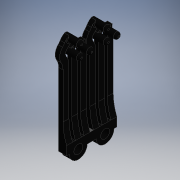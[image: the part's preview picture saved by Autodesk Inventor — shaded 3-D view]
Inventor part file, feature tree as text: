
AUTODESK INVENTOR PART (.ipt)
format: ipt  version: 2016 (Build 200138000, 138)  size: 284,672 bytes
history: native  units: mm (DEFAULTED — no unit token found)
features: other x3, extrude x1, sketch x1
ambient origin geometry x8: Origin, YZ Plane, XZ Plane, XY Plane, X Axis, Y Axis, Z Axis, Center Point
bodies: Solid1 (feature_tree)
feature tree (5):
  other  "Braille Cell.iam"
  other  "Level1_CPY.ipt:1"
  other  "Level1_CPY.ipt:3"
  extrude  "Extrusion1"  Depth=10.0mm TaperAngle=0.0deg
  sketch  "Sketch1"  dims[d0=10.0mm d1=10.0mm d2=0.0mm]
